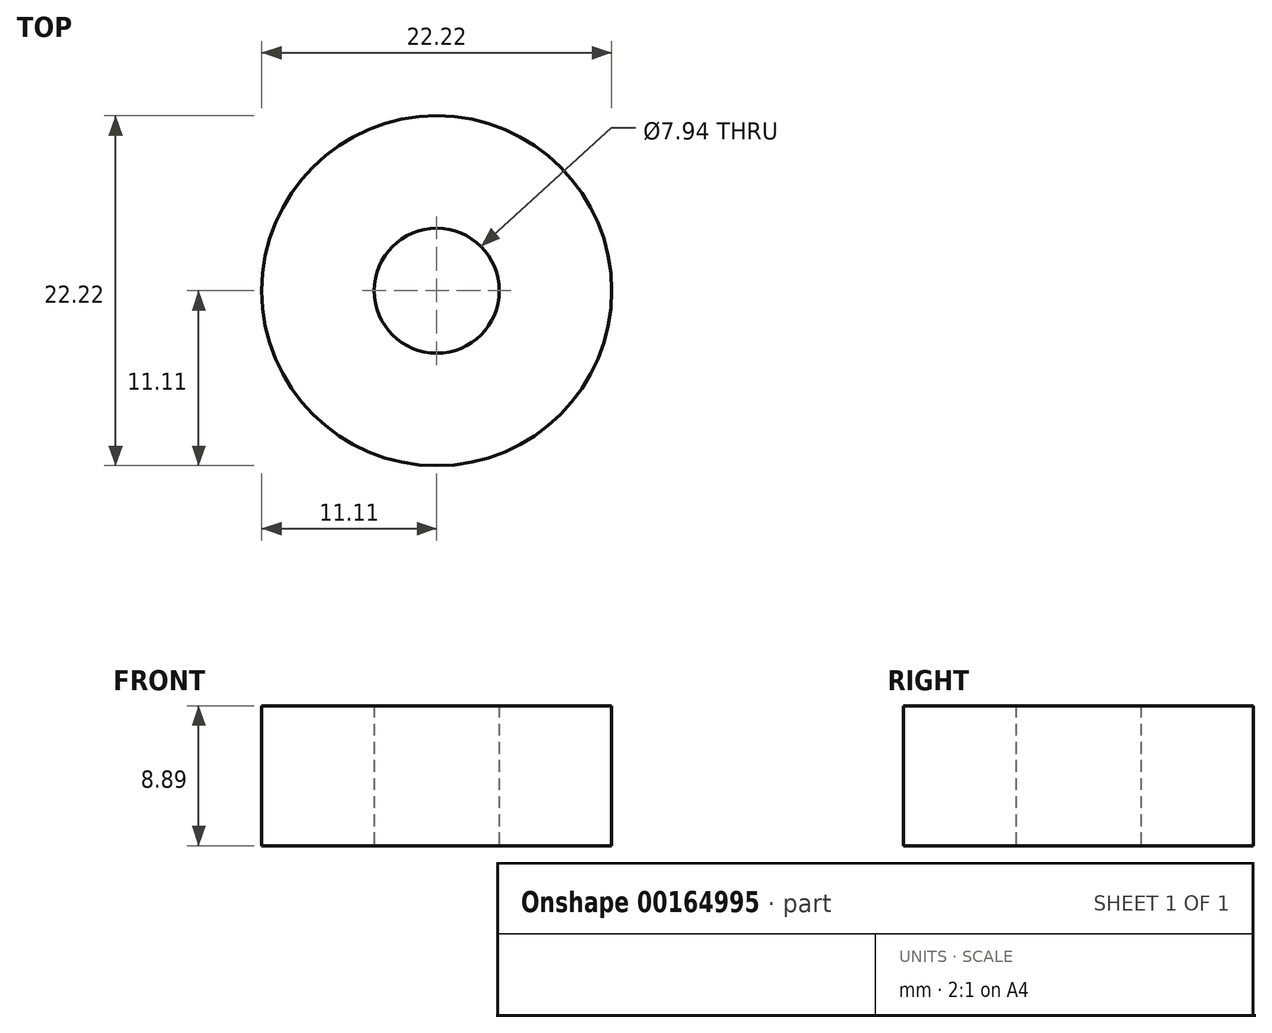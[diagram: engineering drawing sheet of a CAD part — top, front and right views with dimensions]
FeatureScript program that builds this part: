
annotation { "Feature Type Name" : "Feature", "Feature Type Description" : "" }
export const myFeature = defineFeature(function(context is Context, id is Id, definition is map)
    precondition{}
    {
        {
            var Q0;
            Q0=qCreatedBy(makeId("Top.planeOp"),FACE);
            var sketch = newSketch(context, id + "F0", { "sketchPlane" : qUnion([Q0])});
            skCircle(sketch, "E0", {"center": v(0, 0) * mm, "radius": 3.97 * mm});
            skCircle(sketch, "E1", {"center": v(0, 0) * mm, "radius": 11.11 * mm});
            skSolve(sketch);
        }
        {
            var Q0;
            Q0=qSketchRegion(id+"F0",true);
            extrude(context, id + "F1", {"entities" : qUnion([Q0]), "depth" : 8.9 * mm});
        }
    });
